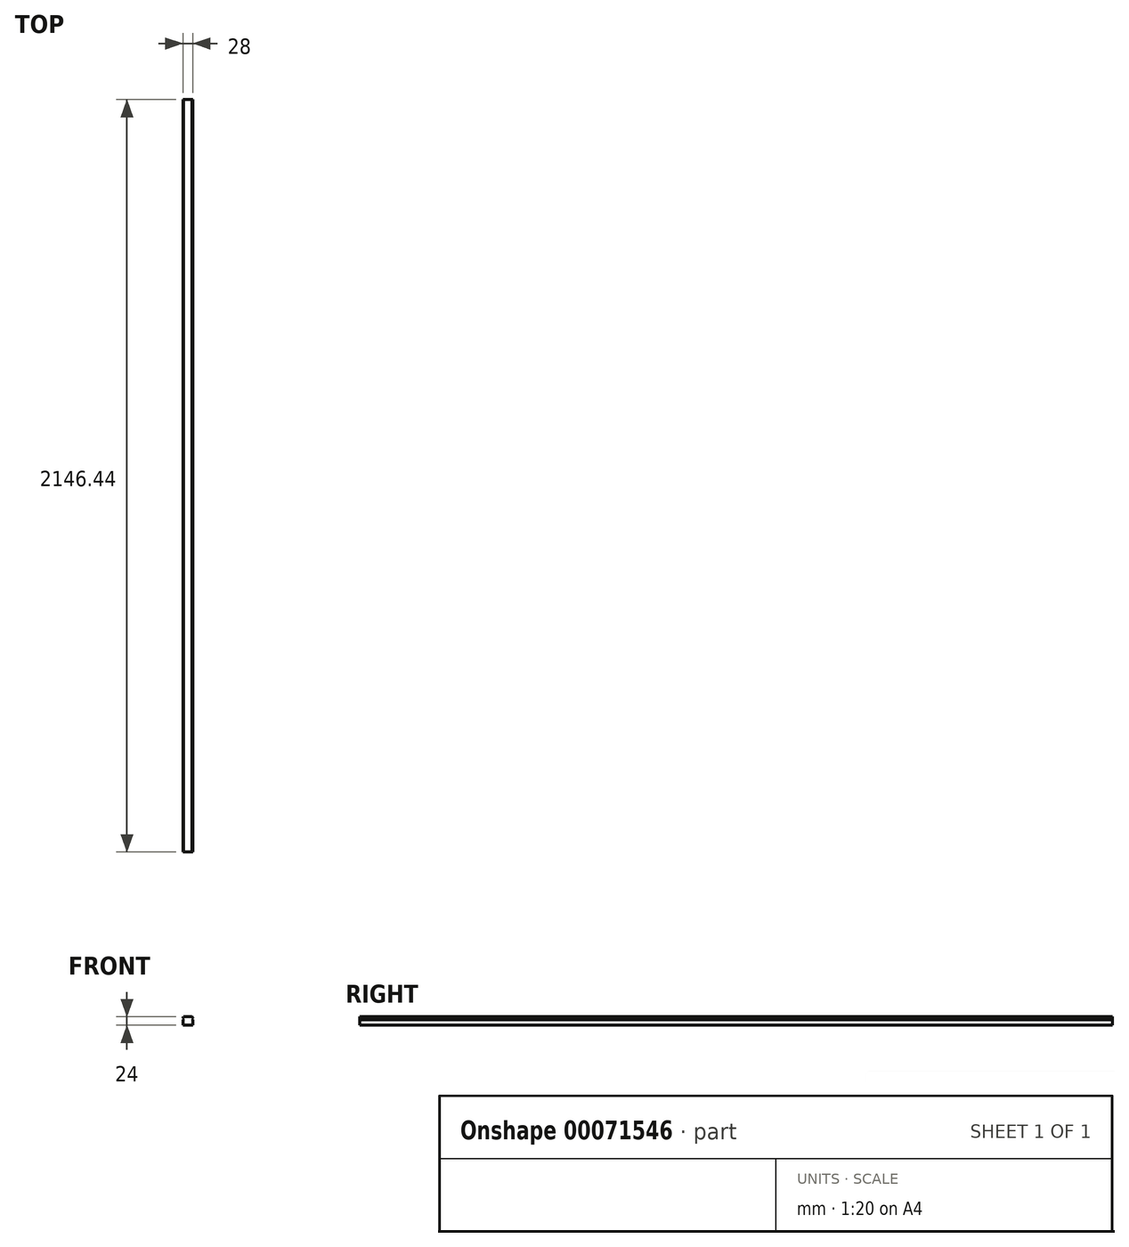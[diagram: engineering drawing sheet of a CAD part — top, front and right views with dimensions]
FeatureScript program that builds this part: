
annotation { "Feature Type Name" : "Feature", "Feature Type Description" : "" }
export const myFeature = defineFeature(function(context is Context, id is Id, definition is map)
    precondition{}
    {
        {
            var Q0;
            Q0=qCreatedBy(makeId("Front.planeOp"),FACE);
            var sketch = newSketch(context, id + "F0", { "sketchPlane" : qUnion([Q0])});
            skLineSegment(sketch, "E0.bottom", {"start": v(-9.9, 12.6) * mm, "end": v(13.87, 12.6) * mm});
            skLineSegment(sketch, "E0.top", {"start": v(-12.01, -11.4) * mm, "end": v(15.99, -11.4) * mm});
            skLineSegment(sketch, "E0.left", {"start": v(-12.01, 10.49) * mm, "end": v(-12.01, 9.49) * mm});
            skLineSegment(sketch, "E0.right", {"start": v(15.99, 10.49) * mm, "end": v(15.99, 9.49) * mm});
            skLineSegment(sketch, "E1", {"start": v(-9.9, 12.6) * mm, "end": v(-12.01, 10.49) * mm});
            skLineSegment(sketch, "E2", {"start": v(13.87, 12.6) * mm, "end": v(15.99, 10.49) * mm});
            skLineSegment(sketch, "E3", {"start": v(-12.01, 9.49) * mm, "end": v(-9.18, 6.66) * mm});
            skLineSegment(sketch, "E4", {"start": v(-9.18, 6.66) * mm, "end": v(-12.01, 3.83) * mm});
            skLineSegment(sketch, "E5", {"start": v(15.99, 9.49) * mm, "end": v(13.16, 6.66) * mm});
            skLineSegment(sketch, "E6", {"start": v(13.16, 6.66) * mm, "end": v(15.99, 3.83) * mm});
            skLineSegment(sketch, "E7.trimOffspring", {"start": v(-12.01, 3.83) * mm, "end": v(-12.01, -11.4) * mm});
            skLineSegment(sketch, "E8.trimOffspring", {"start": v(15.99, 3.83) * mm, "end": v(15.99, -11.4) * mm});
            skSolve(sketch);
        }
        {
            var Q0;
            Q0=qSketchRegion(id+"F0",true);
            extrude(context, id + "F1", {"entities" : qUnion([Q0]), "depth" : 2146.44 * mm});
        }
    });
